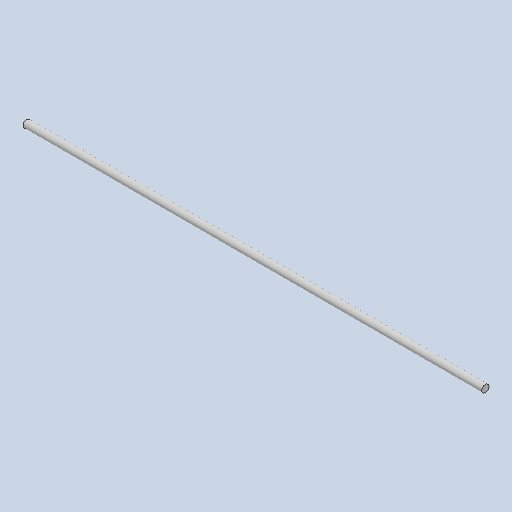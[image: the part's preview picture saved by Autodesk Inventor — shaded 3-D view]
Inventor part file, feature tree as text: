
AUTODESK INVENTOR PART (.ipt)
format: ipt  version: 2023 (Build 270158000, 158)  size: 81,408 bytes
history: native  units: mm
features: extrude x1, sketch x1
ambient origin geometry x8: Origin, YZ Plane, XZ Plane, XY Plane, X Axis, Y Axis, Z Axis, Center Point
bodies: Solid1 (feature_tree)
feature tree (2):
  extrude  "Extrusion1"  Depth=500.0mm TaperAngle=0.0deg
  sketch  "Sketch1"  dims[d0=8.0mm d1=500.0mm d2=0.0mm]
